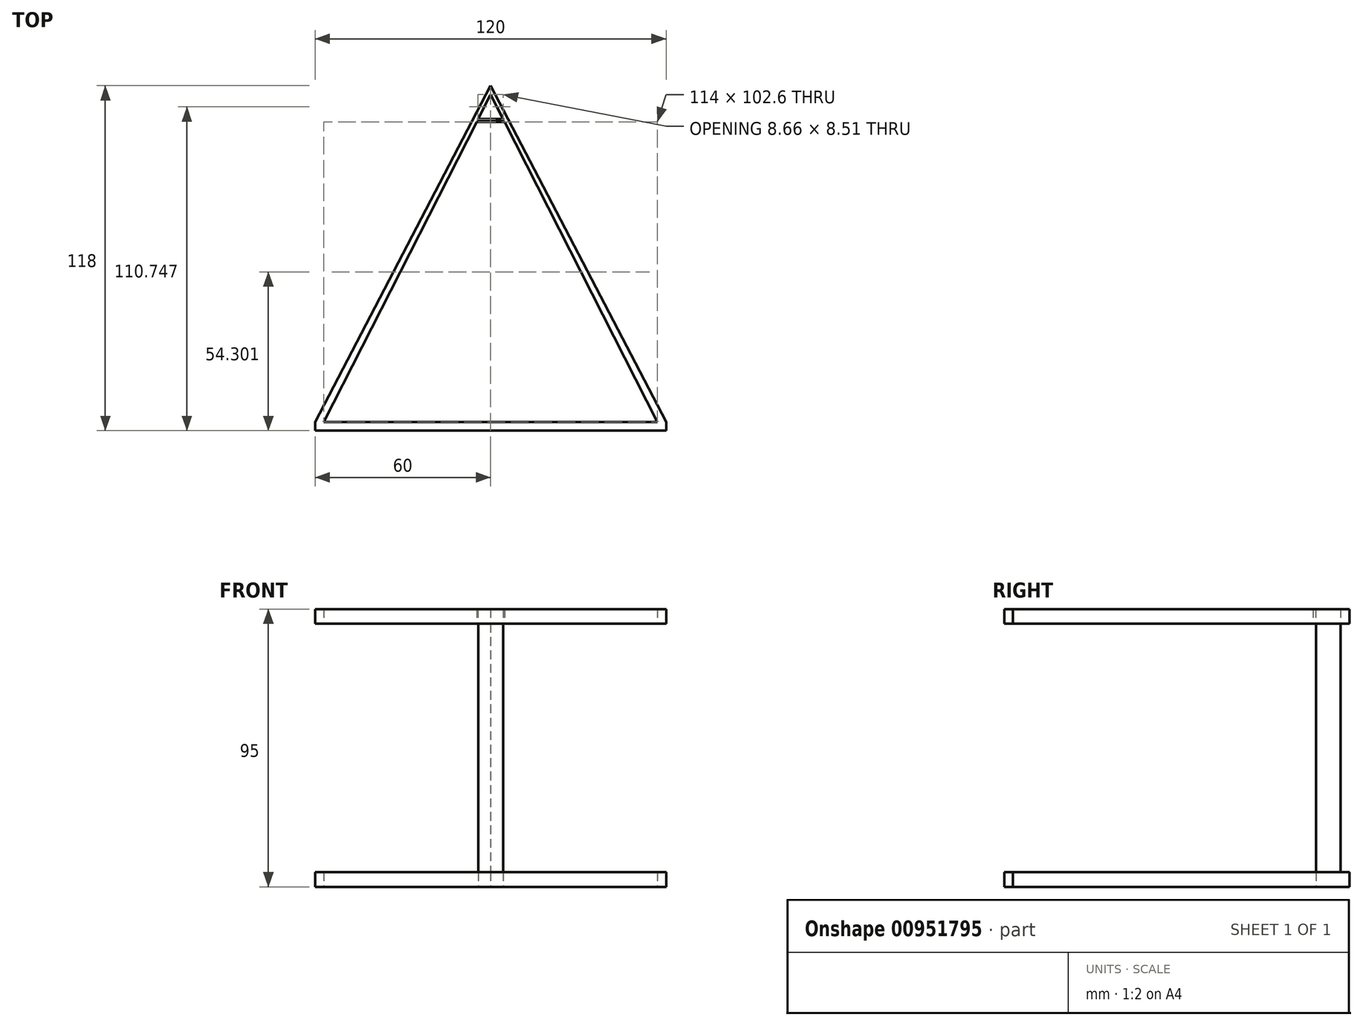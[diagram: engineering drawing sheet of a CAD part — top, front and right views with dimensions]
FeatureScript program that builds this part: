
annotation { "Feature Type Name" : "Feature", "Feature Type Description" : "" }
export const myFeature = defineFeature(function(context is Context, id is Id, definition is map)
    precondition{}
    {
        {
            var Q0;
            Q0=qCreatedBy(makeId("Top.planeOp"),FACE);
            var sketch = newSketch(context, id + "F0", { "sketchPlane" : qUnion([Q0])});
            skLineSegment(sketch, "E0", {"start": v(0, 0) * mm, "end": v(-60, 0) * mm});
            skLineSegment(sketch, "E1", {"start": v(0, 0) * mm, "end": v(60, 0) * mm});
            skLineSegment(sketch, "E2", {"start": v(-60, 0) * mm, "end": v(-60, 3) * mm});
            skLineSegment(sketch, "E3", {"start": v(60, 0) * mm, "end": v(60, 3) * mm});
            skLineSegment(sketch, "E4", {"start": v(60, 3) * mm, "end": v(-60, 3) * mm});
            skLineSegment(sketch, "E5", {"start": v(0, 118) * mm, "end": v(-60, 3) * mm});
            skLineSegment(sketch, "E6", {"start": v(0, 118) * mm, "end": v(60, 3) * mm});
            skLineSegment(sketch, "E7", {"start": v(-60, 3) * mm, "end": v(-57, 3) * mm});
            skLineSegment(sketch, "E8", {"start": v(-57, 3) * mm, "end": v(0, 115) * mm});
            skLineSegment(sketch, "E9", {"start": v(0, 115) * mm, "end": v(57, 3) * mm});
            skSolve(sketch);
        }
        {
            var Q0;
            Q0=makeQuery(id+"F0.imprint","IMPRINT",FACE,{"disambiguationData":[TD([[makeQuery(id+"F0.imprint","IMPRINT",EDGE,{"derivedFrom":sQuery(id+"F0.wireOp",EDGE,"E5")}),1.0]])]});
            var Q1;
            Q1=makeQuery(id+"F0.imprint","IMPRINT",FACE,{"disambiguationData":[TD([[makeQuery(id+"F0.imprint","IMPRINT",EDGE,{"derivedFrom":sQuery(id+"F0.wireOp",EDGE,"E0")}),-1.0]])]});
            extrude(context, id + "F1", {"entities" : qUnion([Q0, Q1]), "depth" : 5 * mm, "offsetDistance" : 25 * mm});
        }
        {
            var Q0;
            Q0=makeQuery(id+"F1.opExtrude","CAP_FACE",FACE,{"disambiguationData":[OSD([sQuery(id+"F0.wireOp",EDGE,"E0"),sQuery(id+"F0.wireOp",EDGE,"E1"),sQuery(id+"F0.wireOp",EDGE,"E2"),sQuery(id+"F0.wireOp",EDGE,"E3"),sQuery(id+"F0.wireOp",EDGE,"E4"),sQuery(id+"F0.wireOp",EDGE,"E5"),sQuery(id+"F0.wireOp",EDGE,"E6"),sQuery(id+"F0.wireOp",EDGE,"E8"),sQuery(id+"F0.wireOp",EDGE,"E9")])],"isStart":false});
            var sketch = newSketch(context, id + "F2", { "sketchPlane" : qUnion([Q0])});
            skLineSegment(sketch, "E10", {"start": v(4.27, 106.61) * mm, "end": v(-4.27, 106.61) * mm});
            skLineSegment(sketch, "E11", {"start": v(-4.27, 106.61) * mm, "end": v(0, 115) * mm});
            skLineSegment(sketch, "E12", {"start": v(0, 115) * mm, "end": v(4.27, 106.61) * mm});
            skSolve(sketch);
        }
        {
            var Q0;
            Q0=makeQuery(id+"F2.imprint","IMPRINT",FACE,{"disambiguationData":[TD([[makeQuery(id+"F2.imprint","IMPRINT",EDGE,{"derivedFrom":sQuery(id+"F2.wireOp",EDGE,"NrCWMD9K-87Or-ZhAE-FyAA-c7GTaB35dpng")}),-1.0]])]});
            var Q1;
            Q1=makeQuery(id+"F2.imprint","IMPRINT",FACE,{"disambiguationData":[TD([[makeQuery(id+"F2.imprint","IMPRINT",EDGE,{"derivedFrom":sQuery(id+"F2.wireOp",EDGE,"E10")}),-1.0]])]});
            extrude(context, id + "F3", {"entities" : qUnion([Q0, Q1]), "operationType" : NewBodyOperationType.ADD, "depth" : 85 * mm, "offsetDistance" : 25 * mm, "hasSecondDirection" : true, "secondDirectionOppositeDirection" : true, "secondDirectionDepth" : 5 * mm});
        }
        {
            var Q0;
            Q0=makeQuery(id+"F3.opExtrude","CAP_FACE",FACE,{"disambiguationData":[OSD([sQuery(id+"F2.wireOp",EDGE,"E10"),sQuery(id+"F2.wireOp",EDGE,"E11"),sQuery(id+"F2.wireOp",EDGE,"E12")])],"isStart":false});
            var sketch = newSketch(context, id + "F4", { "sketchPlane" : qUnion([Q0])});
            skLineSegment(sketch, "E13", {"start": v(0, 115) * mm, "end": v(-57, 3) * mm});
            skLineSegment(sketch, "E14", {"start": v(0, 115) * mm, "end": v(57, 3) * mm});
            skLineSegment(sketch, "E15", {"start": v(57, 3) * mm, "end": v(-57, 3) * mm});
            skLineSegment(sketch, "E16", {"start": v(-57, 3) * mm, "end": v(-60, 3) * mm});
            skLineSegment(sketch, "E17", {"start": v(-60, 3) * mm, "end": v(-60, 0) * mm});
            skLineSegment(sketch, "E18", {"start": v(57, 3) * mm, "end": v(60, 3) * mm});
            skLineSegment(sketch, "E19", {"start": v(60, 3) * mm, "end": v(60, 0) * mm});
            skLineSegment(sketch, "E20", {"start": v(60, 0) * mm, "end": v(-60, 0) * mm});
            skLineSegment(sketch, "E21", {"start": v(0, 115) * mm, "end": v(0, 118) * mm});
            skLineSegment(sketch, "E22", {"start": v(0, 118) * mm, "end": v(-60, 3) * mm});
            skLineSegment(sketch, "E23", {"start": v(0, 118) * mm, "end": v(60, 3) * mm});
            skSolve(sketch);
        }
        {
            var Q0;
            {var subQ3=sQuery(id+"F4.wireOp",EDGE,"E18");Q0=makeQuery(id+"F4.imprint","IMPRINT",FACE,{"disambiguationData":[TD([[makeQuery(id+"F4.imprint","IMPRINT",EDGE,{"derivedFrom":subQ3}),1.0]])]});}
            var Q1;
            {var subQ3=sQuery(id+"F4.wireOp",EDGE,"E16");Q1=makeQuery(id+"F4.imprint","IMPRINT",FACE,{"disambiguationData":[TD([[makeQuery(id+"F4.imprint","IMPRINT",EDGE,{"derivedFrom":subQ3}),-1.0]])]});}
            var Q2;
            Q2=makeQuery(id+"F4.imprint","IMPRINT",FACE,{"disambiguationData":[TD([[makeQuery(id+"F4.imprint","IMPRINT",EDGE,{"derivedFrom":sQuery(id+"F4.wireOp",EDGE,"E15")}),1.0]])]});
            extrude(context, id + "F5", {"entities" : qUnion([Q0, Q1, Q2]), "depth" : 5 * mm, "offsetDistance" : 25 * mm});
        }
        {
            var Q0;
            Q0=makeQuery(id+"F5.opExtrude","CAP_FACE",FACE,{"disambiguationData":[OSD([sQuery(id+"F4.wireOp",EDGE,"E13"),sQuery(id+"F4.wireOp",EDGE,"E14"),sQuery(id+"F4.wireOp",EDGE,"E15"),sQuery(id+"F4.wireOp",EDGE,"E17"),sQuery(id+"F4.wireOp",EDGE,"E19"),sQuery(id+"F4.wireOp",EDGE,"E20"),sQuery(id+"F4.wireOp",EDGE,"E22"),sQuery(id+"F4.wireOp",EDGE,"E23")])],"isStart":true});
            var sketch = newSketch(context, id + "F6", { "sketchPlane" : qUnion([Q0])});
            skLineSegment(sketch, "E24", {"start": v(-4.33, -106.5) * mm, "end": v(4.33, -106.5) * mm});
            skLineSegment(sketch, "E25", {"start": v(4.33, -106.5) * mm, "end": v(4.78, -105.6) * mm});
            skLineSegment(sketch, "E26", {"start": v(4.78, -105.6) * mm, "end": v(-4.78, -105.6) * mm});
            skLineSegment(sketch, "E27", {"start": v(-4.78, -105.6) * mm, "end": v(-4.33, -106.5) * mm});
            skSolve(sketch);
        }
        {
            var Q0;
            Q0=makeQuery(id+"F6.imprint","IMPRINT",FACE,{"disambiguationData":[TD([[makeQuery(id+"F6.imprint","IMPRINT",EDGE,{"derivedFrom":sQuery(id+"F6.wireOp",EDGE,"E24")}),1.0]])]});
            extrude(context, id + "F7", {"entities" : qUnion([Q0]), "operationType" : NewBodyOperationType.ADD, "oppositeDirection" : true, "depth" : 5 * mm, "offsetDistance" : 25 * mm});
        }
    });
